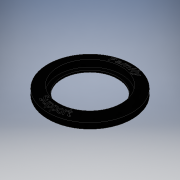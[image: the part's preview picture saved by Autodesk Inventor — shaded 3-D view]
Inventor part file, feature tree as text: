
AUTODESK INVENTOR PART (.ipt)
format: ipt  version: 2016 (Build 200138000, 138)  size: 537,600 bytes
history: native  units: in
note: dims shown in document units (in); Inventor stores cm internally (conversion verified against a paired STEP export)
features: sketch x2, projected_geometry x2, revolve x1, extrude x1
ambient origin geometry x8: Origin, YZ Plane, XZ Plane, XY Plane, X Axis, Y Axis, Z Axis, Center Point
bodies: Solid1 (feature_tree)
feature tree (6):
  revolve  "Revolution1"  [1 undecoded]
  extrude  "Extrusion1"  Depth=0.1in
  sketch  "Sketch1"  dims[d0=0.8265in d1=0.175in]
  sketch  "Sketch2"  dims[d2=0.05in d3=0.1in d4=0.15in d5=0.275in d6=90.0deg d7=1.0in d8=0.0in]
  projected_geometry  "Projected Loop1"
  projected_geometry  "Projected Loop2"
note: 1 required parameter value undecoded (feature->parameter linkage not recoverable at this tier; creation-order binding heuristic only, values carry confidence <= 0.55)
